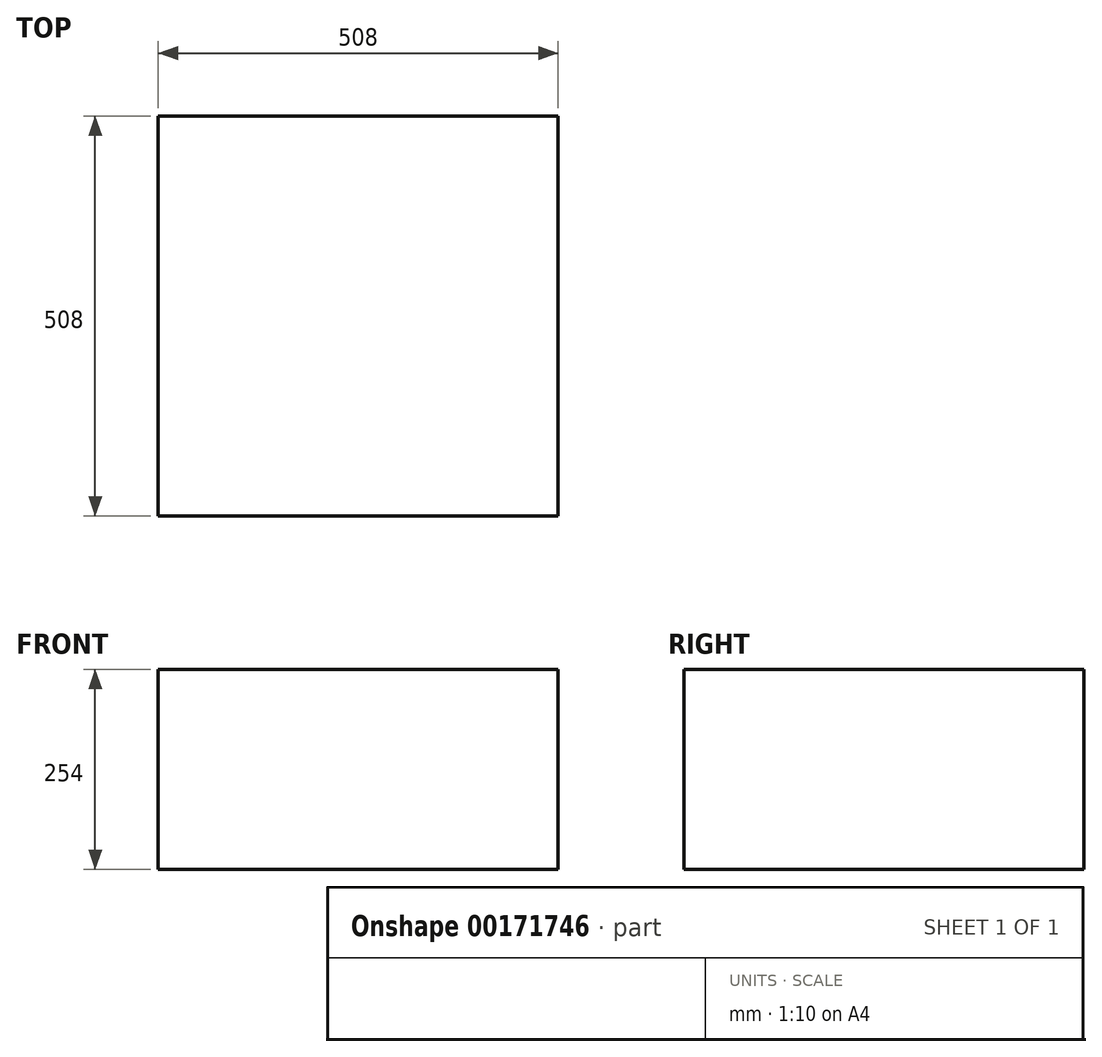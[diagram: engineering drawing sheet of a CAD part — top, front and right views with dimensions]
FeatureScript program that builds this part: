
annotation { "Feature Type Name" : "Feature", "Feature Type Description" : "" }
export const myFeature = defineFeature(function(context is Context, id is Id, definition is map)
    precondition{}
    {
        {
            var Q0;
            Q0=qCreatedBy(makeId("Top.planeOp"),FACE);
            var sketch = newSketch(context, id + "F0", { "sketchPlane" : qUnion([Q0])});
            skLineSegment(sketch, "E0.bottom", {"start": v(0, 0) * mm, "end": v(508, 0) * mm});
            skLineSegment(sketch, "E0.top", {"start": v(0, -508) * mm, "end": v(508, -508) * mm});
            skLineSegment(sketch, "E0.left", {"start": v(0, 0) * mm, "end": v(0, -508) * mm});
            skLineSegment(sketch, "E0.right", {"start": v(508, 0) * mm, "end": v(508, -508) * mm});
            skSolve(sketch);
        }
        {
            var Q0;
            Q0 = qSketchRegion(id + "F0", true);
            extrude(context, id + "F1", {"entities" : qUnion([Q0]), "depth" : 254 * mm});
        }
    });
